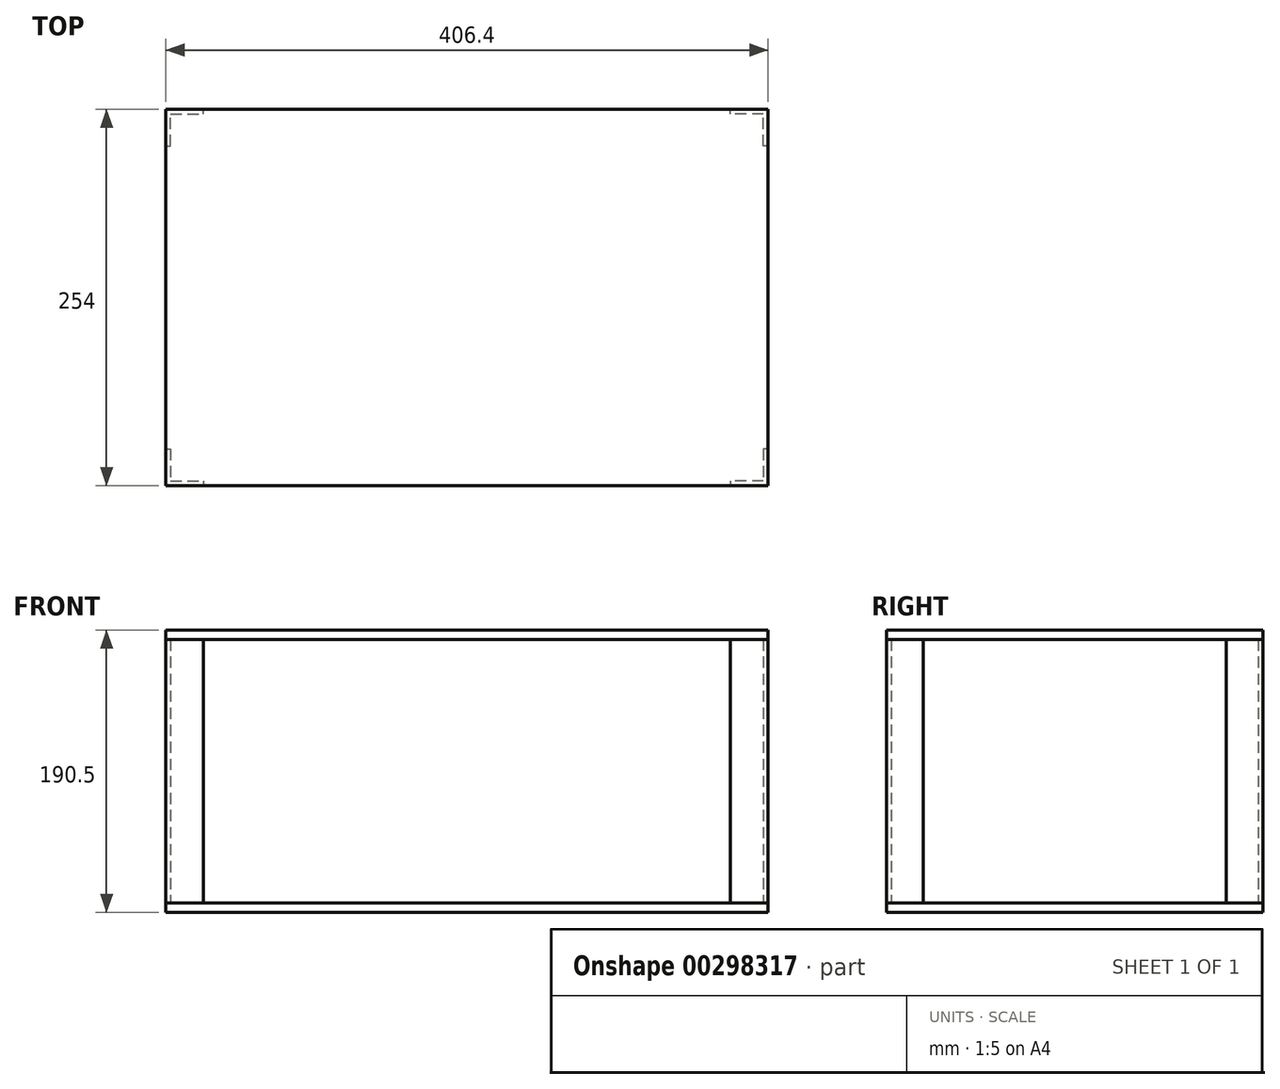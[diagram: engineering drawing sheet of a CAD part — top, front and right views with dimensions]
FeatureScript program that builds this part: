
annotation { "Feature Type Name" : "Feature", "Feature Type Description" : "" }
export const myFeature = defineFeature(function(context is Context, id is Id, definition is map)
    precondition{}
    {
        {
            var Q0;
            Q0=qCreatedBy(makeId("Top.planeOp"),FACE);
            var sketch = newSketch(context, id + "F0", { "sketchPlane" : qUnion([Q0])});
            skLineSegment(sketch, "E0.bottom", {"start": v(-203.2, 127) * mm, "end": v(203.2, 127) * mm});
            skLineSegment(sketch, "E0.top", {"start": v(-203.2, -127) * mm, "end": v(203.2, -127) * mm});
            skLineSegment(sketch, "E0.left", {"start": v(-203.2, 127) * mm, "end": v(-203.2, -127) * mm});
            skLineSegment(sketch, "E0.right", {"start": v(203.2, 127) * mm, "end": v(203.2, -127) * mm});
            skPoint(sketch, "E0.middle", {"position": v(0, 0) * mm});
            skSolve(sketch);
        }
        {
            var Q0;
            Q0 = qSketchRegion(id + "F0", true);
            extrude(context, id + "F1", {"entities" : qUnion([Q0]), "depth" : 6.35 * mm});
        }
        {
            var Q0;
            Q0=makeQuery(id+"F1.opExtrude","CAP_FACE",FACE,{"disambiguationData":[OSD([sQuery(id+"F0.wireOp",EDGE,"E0.bottom"),sQuery(id+"F0.wireOp",EDGE,"E0.top"),sQuery(id+"F0.wireOp",EDGE,"E0.left"),sQuery(id+"F0.wireOp",EDGE,"E0.right")])],"isStart":false});
            var sketch = newSketch(context, id + "F2", { "sketchPlane" : qUnion([Q0])});
            skLineSegment(sketch, "E1", {"start": v(0, 0) * mm, "end": v(0, -24.77) * mm});
            skLineSegment(sketch, "E2", {"start": v(0, 0) * mm, "end": v(25.4, 0) * mm});
            skLineSegment(sketch, "E3", {"start": v(0, -24.77) * mm, "end": v(3.18, -24.77) * mm});
            skLineSegment(sketch, "E4", {"start": v(3.18, -24.77) * mm, "end": v(3.17, -3.18) * mm});
            skLineSegment(sketch, "E5", {"start": v(3.17, -3.18) * mm, "end": v(25.4, -3.18) * mm});
            skLineSegment(sketch, "E6", {"start": v(25.4, -3.18) * mm, "end": v(25.4, 0) * mm});
            skSolve(sketch);
        }
        {
            var Q0;
            Q0 = qSketchRegion(id + "F2", true);
            extrude(context, id + "F3", {"entities" : qUnion([Q0]), "depth" : 177.8 * mm});
        }
        {
            var Q0;
            Q0=makeQuery(id+"F3.opExtrude","SWEPT_BODY",BODY,{"disambiguationData":[OSD([sQuery(id+"F2.wireOp",EDGE,"E1"),sQuery(id+"F2.wireOp",EDGE,"E2"),sQuery(id+"F2.wireOp",EDGE,"E3"),sQuery(id+"F2.wireOp",EDGE,"E4"),sQuery(id+"F2.wireOp",EDGE,"E5"),sQuery(id+"F2.wireOp",EDGE,"E6")])]});
            var Q1;
            Q1=makeQuery(id+"F1.opExtrude","CAP_VERTEX",VERTEX,{"disambiguationData":[OSD([sQuery(id+"F0.wireOp",EDGE,"E0.bottom"),sQuery(id+"F0.wireOp",EDGE,"E0.left")])],"isStart":false});
            transform(context, id + "F4", {"entities" : qUnion([Q0]), "transformType" : TransformType.TRANSLATION_3D, "dx" : -203.2 * mm, "dy" : 127 * mm, "dz" : 0 * mm, "makeCopy" : false});
        }
        {
            var Q0;
            Q0=makeQuery(id+"F3.opExtrude","SWEPT_BODY",BODY,{"disambiguationData":[OSD([sQuery(id+"F2.wireOp",EDGE,"E1"),sQuery(id+"F2.wireOp",EDGE,"E2"),sQuery(id+"F2.wireOp",EDGE,"E3"),sQuery(id+"F2.wireOp",EDGE,"E4"),sQuery(id+"F2.wireOp",EDGE,"E5"),sQuery(id+"F2.wireOp",EDGE,"E6")])]});
            var Q1;
            Q1=qCreatedBy(makeId("Right.planeOp"),FACE);
            mirror(context, id + "F5", {"entities" : qUnion([Q0]), "mirrorPlane" : qUnion([Q1])});
        }
        {
            var Q0;
            Q0=makeQuery(id+"F3.opExtrude","SWEPT_BODY",BODY,{"disambiguationData":[OSD([sQuery(id+"F2.wireOp",EDGE,"E1"),sQuery(id+"F2.wireOp",EDGE,"E2"),sQuery(id+"F2.wireOp",EDGE,"E3"),sQuery(id+"F2.wireOp",EDGE,"E4"),sQuery(id+"F2.wireOp",EDGE,"E5"),sQuery(id+"F2.wireOp",EDGE,"E6")])]});
            var Q1;
            Q1=makeQuery(id+"F5.opPattern","COPY",BODY,{"derivedFrom":makeQuery(id+"F3.opExtrude","SWEPT_BODY",BODY,{"disambiguationData":[OSD([sQuery(id+"F2.wireOp",EDGE,"E1"),sQuery(id+"F2.wireOp",EDGE,"E2"),sQuery(id+"F2.wireOp",EDGE,"E3"),sQuery(id+"F2.wireOp",EDGE,"E4"),sQuery(id+"F2.wireOp",EDGE,"E5"),sQuery(id+"F2.wireOp",EDGE,"E6")])]}),"instanceName":"1"});
            var Q2;
            Q2=qCreatedBy(makeId("Front.planeOp"),FACE);
            mirror(context, id + "F6", {"entities" : qUnion([Q0, Q1]), "mirrorPlane" : qUnion([Q2])});
        }
        {
            var Q0;
            Q0=makeQuery(id+"F3.opExtrude","CAP_FACE",FACE,{"disambiguationData":[OSD([sQuery(id+"F2.wireOp",EDGE,"E1"),sQuery(id+"F2.wireOp",EDGE,"E2"),sQuery(id+"F2.wireOp",EDGE,"E3"),sQuery(id+"F2.wireOp",EDGE,"E4"),sQuery(id+"F2.wireOp",EDGE,"E5"),sQuery(id+"F2.wireOp",EDGE,"E6")])],"isStart":false});
            var sketch = newSketch(context, id + "F7", { "sketchPlane" : qUnion([Q0])});
            skLineSegment(sketch, "E7.bottom", {"start": v(-203.2, 127) * mm, "end": v(203.2, 127) * mm});
            skLineSegment(sketch, "E7.top", {"start": v(-203.2, -127) * mm, "end": v(203.2, -127) * mm});
            skLineSegment(sketch, "E7.left", {"start": v(-203.2, 127) * mm, "end": v(-203.2, -127) * mm});
            skLineSegment(sketch, "E7.right", {"start": v(203.2, 127) * mm, "end": v(203.2, -127) * mm});
            skPoint(sketch, "E7.middle", {"position": v(0, 0) * mm});
            skSolve(sketch);
        }
        {
            var Q0;
            Q0 = qSketchRegion(id + "F7", true);
            extrude(context, id + "F8", {"entities" : qUnion([Q0]), "depth" : 6.35 * mm});
        }
    });
